# Revit family: 873-00-002-DN1100-1200
name_source: partatom
category: Generic Models
units: mm (PartAtom-declared; Revit-internal decimal feet)

## family parameters
Always vertical = Yes
Can host rebar = No
Cut with Voids When Loaded = No
Part Type = Normal
Room Calculation Point = No
Round Connector Dimension = Use Diameter
Shared = No
Work Plane-Based = No

## types (2) — shared parameters
873-1100-00-741000 = DN1100_PN25
873-1200-00-741000 = DN1200_PN25
Angle = 22.50°
Body_Wallthicknss = 10 mm  [stored 0.0328084 ft]
Description_ = AVK DISMANTLING JOINT
Flange_thickness = 20 mm  [stored 0.0656168 ft]
Search_table = 873-00-002-DN1100-1200
T = 52 mm
URL product pages = https://www.avkvalves.com

## per-type parameters (varying)
| type | A | DN | Id(Radius) | L | d1 | d2 |
| DN1100 | 395 mm  [stored 1.29593 ft] | 1100 mm  [stored 3.60892 ft] | 550 mm | 670 mm  [stored 2.19816 ft] | 1310 mm  [stored 4.2979 ft] | 710 mm |
| DN1200 | 425 mm  [stored 1.39436 ft] | 1200 mm  [stored 3.93701 ft] | 600 mm | 700 mm  [stored 2.29659 ft] | 1420 mm | 765 mm  [stored 2.50984 ft] |

note: [stored X ft] marks values corroborated as IEEE doubles in the binary element streams (Revit-internal decimal feet)

## geometry (parser evidence)
native form markers: Sweep x5
no freeform markers — native parametric forms only
